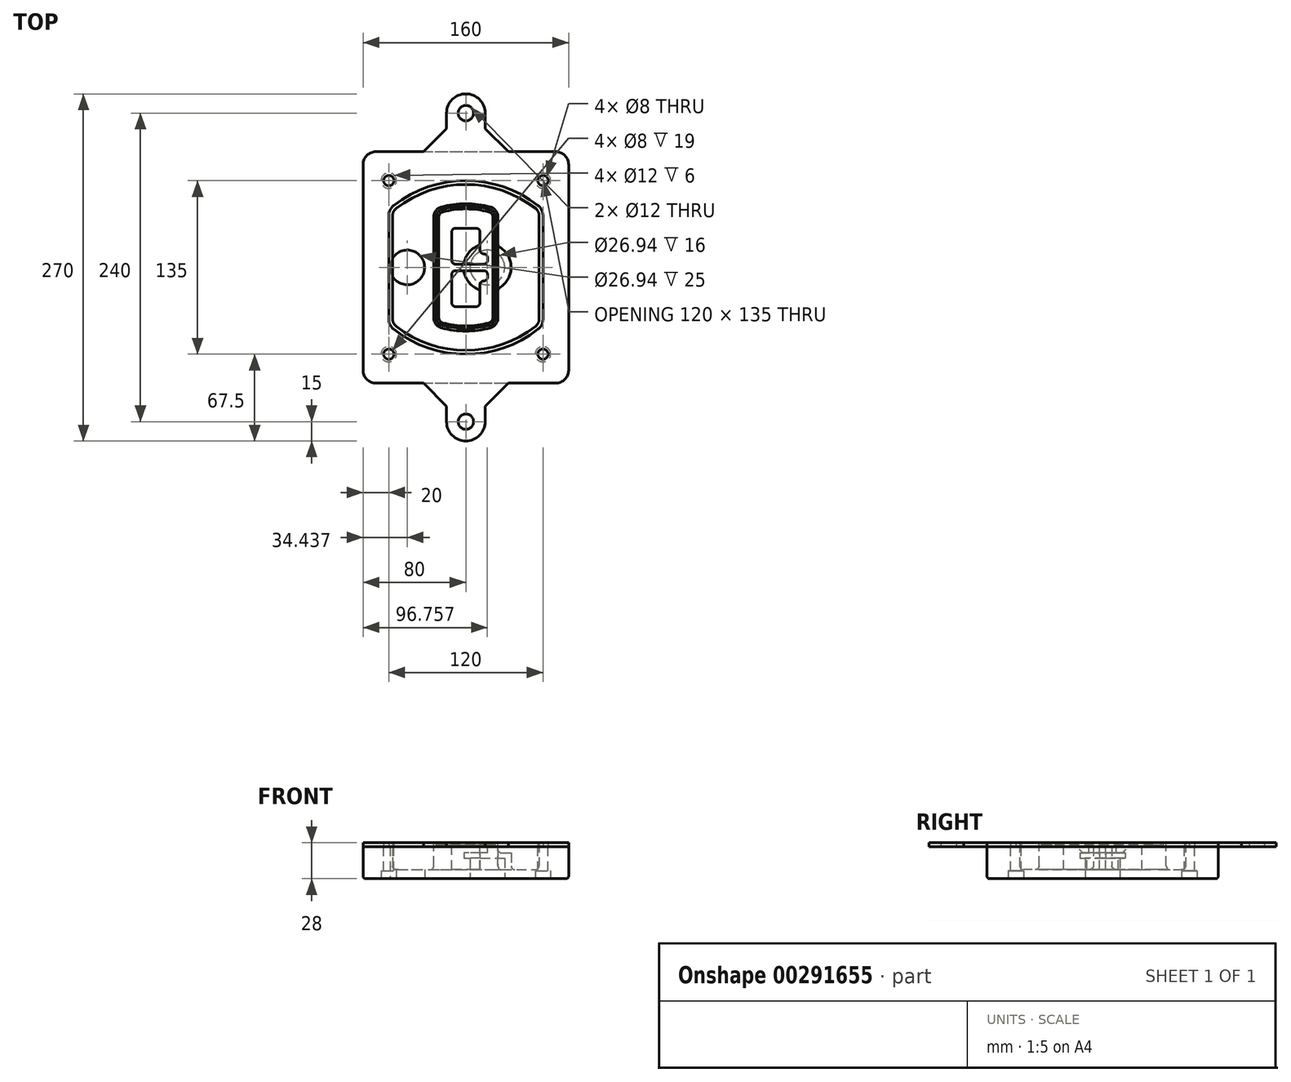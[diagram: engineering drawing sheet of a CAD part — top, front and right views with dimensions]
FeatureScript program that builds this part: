
annotation { "Feature Type Name" : "Feature", "Feature Type Description" : "" }
export const myFeature = defineFeature(function(context is Context, id is Id, definition is map)
    precondition{}
    {
        {
            var Q0;
            Q0=qCreatedBy(makeId("Top.planeOp"),FACE);
            var sketch = newSketch(context, id + "F0", { "sketchPlane" : qUnion([Q0])});
            skPoint(sketch, "E0.rect.middle", {"position": v(0, 0) * mm});
            skLineSegment(sketch, "E1.bottom", {"start": v(-70, -90) * mm, "end": v(70, -90) * mm});
            skLineSegment(sketch, "E1.top", {"start": v(-70, 90) * mm, "end": v(70, 90) * mm});
            skLineSegment(sketch, "E1.left", {"start": v(-80, -80) * mm, "end": v(-80, 80) * mm});
            skLineSegment(sketch, "E1.right", {"start": v(80, -80) * mm, "end": v(80, 80) * mm});
            skLineSegment(sketch, "E2", {"start": v(-80, 90) * mm, "end": v(80, -90) * mm, "construction": true});
            skLineSegment(sketch, "E3", {"start": v(80, 90) * mm, "end": v(-80, -90) * mm, "construction": true});
            skCircle(sketch, "E4", {"center": v(-60, 67.5) * mm, "radius": 4 * mm});
            skCircle(sketch, "E5", {"center": v(60, 67.5) * mm, "radius": 4 * mm});
            skCircle(sketch, "E6", {"center": v(60, -67.5) * mm, "radius": 4 * mm});
            skCircle(sketch, "E7", {"center": v(-60, -67.5) * mm, "radius": 4 * mm});
            skLineSegment(sketch, "E8", {"start": v(-60, 67.5) * mm, "end": v(60, 67.5) * mm, "construction": true});
            skLineSegment(sketch, "E9", {"start": v(60, 67.5) * mm, "end": v(60, -67.5) * mm, "construction": true});
            skLineSegment(sketch, "E10", {"start": v(60, -67.5) * mm, "end": v(-60, -67.5) * mm, "construction": true});
            skLineSegment(sketch, "E11", {"start": v(-60, -67.5) * mm, "end": v(-60, 67.5) * mm, "construction": true});
            skLineSegment(sketch, "E12", {"start": v(-60, 40.3) * mm, "end": v(-60, -40.3) * mm});
            skLineSegment(sketch, "E13", {"start": v(60, 40.3) * mm, "end": v(60, -40.3) * mm});
            skArc(sketch, "E14", {"start": v(56.15, 48.18) * mm, "mid": v(0, 67.5) * mm, "end": v(-56.15, 48.18) * mm});
            skArc(sketch, "E15", {"start": v(-56.15, -48.18) * mm, "mid": v(0, -67.5) * mm, "end": v(56.15, -48.18) * mm});
            skLineSegment(sketch, "E16", {"start": v(-60, 0) * mm, "end": v(60, 0) * mm, "construction": true});
            skPoint(sketch, "E17.visualSharp", {"position": v(-60, -45) * mm});
            skArc(sketch, "E17.filletArc", {"start": v(-60, -40.3) * mm, "mid": v(-58.99, -44.68) * mm, "end": v(-56.15, -48.18) * mm});
            skPoint(sketch, "E18.visualSharp", {"position": v(-60, 45) * mm});
            skArc(sketch, "E18.filletArc", {"start": v(-56.15, 48.18) * mm, "mid": v(-58.99, 44.68) * mm, "end": v(-60, 40.3) * mm});
            skPoint(sketch, "E19.visualSharp", {"position": v(60, 45) * mm});
            skArc(sketch, "E19.filletArc", {"start": v(60, 40.3) * mm, "mid": v(58.99, 44.68) * mm, "end": v(56.15, 48.18) * mm});
            skPoint(sketch, "E20.visualSharp", {"position": v(60, -45) * mm});
            skArc(sketch, "E20.filletArc", {"start": v(56.15, -48.18) * mm, "mid": v(58.99, -44.68) * mm, "end": v(60, -40.3) * mm});
            skPoint(sketch, "E21.visualSharp", {"position": v(-80, 90) * mm});
            skArc(sketch, "E21.filletArc", {"start": v(-70, 90) * mm, "mid": v(-77.07, 87.07) * mm, "end": v(-80, 80) * mm});
            skPoint(sketch, "E22.visualSharp", {"position": v(80, 90) * mm});
            skArc(sketch, "E22.filletArc", {"start": v(80, 80) * mm, "mid": v(77.07, 87.07) * mm, "end": v(70, 90) * mm});
            skPoint(sketch, "E23.visualSharp", {"position": v(80, -90) * mm});
            skArc(sketch, "E23.filletArc", {"start": v(70, -90) * mm, "mid": v(77.07, -87.07) * mm, "end": v(80, -80) * mm});
            skPoint(sketch, "E24.visualSharp", {"position": v(-80, -90) * mm});
            skArc(sketch, "E24.filletArc", {"start": v(-80, -80) * mm, "mid": v(-77.07, -87.07) * mm, "end": v(-70, -90) * mm});
            skArc(sketch, "E25.0", {"start": v(57, 40.3) * mm, "mid": v(56.3, 43.36) * mm, "end": v(54.3, 45.81) * mm});
            skLineSegment(sketch, "E25.1", {"start": v(57, 40.3) * mm, "end": v(57, -40.3) * mm});
            skArc(sketch, "E25.2", {"start": v(54.3, -45.81) * mm, "mid": v(56.3, -43.36) * mm, "end": v(57, -40.3) * mm});
            skArc(sketch, "E25.3", {"start": v(-54.3, -45.81) * mm, "mid": v(0, -64.5) * mm, "end": v(54.3, -45.81) * mm});
            skArc(sketch, "E25.4", {"start": v(-57, -40.3) * mm, "mid": v(-56.3, -43.36) * mm, "end": v(-54.3, -45.81) * mm});
            skArc(sketch, "E25.5", {"start": v(54.3, 45.81) * mm, "mid": v(0, 64.5) * mm, "end": v(-54.3, 45.81) * mm});
            skLineSegment(sketch, "E25.6", {"start": v(-57, 40.3) * mm, "end": v(-57, -40.3) * mm});
            skArc(sketch, "E25.7", {"start": v(-54.3, 45.81) * mm, "mid": v(-56.3, 43.36) * mm, "end": v(-57, 40.3) * mm});
            skArc(sketch, "E26.0", {"start": v(-58.62, 51.33) * mm, "mid": v(-62.58, 46.43) * mm, "end": v(-64, 40.3) * mm});
            skArc(sketch, "E26.1", {"start": v(58.62, 51.33) * mm, "mid": v(0, 71.5) * mm, "end": v(-58.62, 51.33) * mm});
            skArc(sketch, "E26.2", {"start": v(64, 40.3) * mm, "mid": v(62.58, 46.43) * mm, "end": v(58.62, 51.33) * mm});
            skLineSegment(sketch, "E26.3", {"start": v(64, 40.3) * mm, "end": v(64, -40.3) * mm});
            skArc(sketch, "E26.4", {"start": v(58.62, -51.33) * mm, "mid": v(62.58, -46.43) * mm, "end": v(64, -40.3) * mm});
            skLineSegment(sketch, "E26.5", {"start": v(-64, 40.3) * mm, "end": v(-64, -40.3) * mm});
            skArc(sketch, "E26.6", {"start": v(-58.62, -51.33) * mm, "mid": v(0, -71.5) * mm, "end": v(58.62, -51.33) * mm});
            skArc(sketch, "E26.7", {"start": v(-64, -40.3) * mm, "mid": v(-62.58, -46.43) * mm, "end": v(-58.62, -51.33) * mm});
            skSolve(sketch);
        }
        {
            var Q0;
            Q0=makeQuery(id+"F0.imprint","IMPRINT",FACE,{"disambiguationData":[TD([[makeQuery(id+"F0.imprint","IMPRINT",EDGE,{"derivedFrom":sQuery(id+"F0.wireOp",EDGE,"E1.bottom")}),1.0]])]});
            var Q1;
            Q1=makeQuery(id+"F0.imprint","IMPRINT",FACE,{"disambiguationData":[TD([[makeQuery(id+"F0.imprint","IMPRINT",EDGE,{"derivedFrom":sQuery(id+"F0.wireOp",EDGE,"E12")}),1.0]])]});
            var Q2;
            Q2=makeQuery(id+"F0.imprint","IMPRINT",FACE,{"disambiguationData":[TD([[makeQuery(id+"F0.imprint","IMPRINT",EDGE,{"derivedFrom":sQuery(id+"F0.wireOp",EDGE,"E25.0")}),1.0]])]});
            var Q3;
            Q3=makeQuery(id+"F0.imprint","IMPRINT",FACE,{"disambiguationData":[TD([[makeQuery(id+"F0.imprint","IMPRINT",EDGE,{"derivedFrom":sQuery(id+"F0.wireOp",EDGE,"E12")}),-1.0]])]});
            extrude(context, id + "F1", {"entities" : qUnion([Q0, Q1, Q2, Q3]), "oppositeDirection" : true, "depth" : 25 * mm});
        }
        {
            var Q0;
            Q0=makeQuery(id+"F0.imprint","IMPRINT",FACE,{"disambiguationData":[TD([[makeQuery(id+"F0.imprint","IMPRINT",EDGE,{"derivedFrom":sQuery(id+"F0.wireOp",EDGE,"E12")}),1.0]])]});
            extrude(context, id + "F2", {"entities" : qUnion([Q0]), "operationType" : NewBodyOperationType.ADD, "depth" : 3 * mm});
        }
        {
            var Q0;
            Q0=makeQuery(id+"F0.imprint","IMPRINT",FACE,{"disambiguationData":[TD([[makeQuery(id+"F0.imprint","IMPRINT",EDGE,{"derivedFrom":sQuery(id+"F0.wireOp",EDGE,"E25.0")}),1.0]])]});
            extrude(context, id + "F3", {"entities" : qUnion([Q0]), "operationType" : NewBodyOperationType.REMOVE, "oppositeDirection" : true, "depth" : 18 * mm});
        }
        {
            var Q0;
            Q0=makeQuery(id+"F2.opExtrude","CAP_FACE",FACE,{"disambiguationData":[OSD([sQuery(id+"F0.wireOp",EDGE,"E12"),sQuery(id+"F0.wireOp",EDGE,"E13"),sQuery(id+"F0.wireOp",EDGE,"E14"),sQuery(id+"F0.wireOp",EDGE,"E15"),sQuery(id+"F0.wireOp",EDGE,"E17.filletArc"),sQuery(id+"F0.wireOp",EDGE,"E18.filletArc"),sQuery(id+"F0.wireOp",EDGE,"E19.filletArc"),sQuery(id+"F0.wireOp",EDGE,"E20.filletArc"),sQuery(id+"F0.wireOp",EDGE,"E25.0"),sQuery(id+"F0.wireOp",EDGE,"E25.1"),sQuery(id+"F0.wireOp",EDGE,"E25.2"),sQuery(id+"F0.wireOp",EDGE,"E25.3"),sQuery(id+"F0.wireOp",EDGE,"E25.4"),sQuery(id+"F0.wireOp",EDGE,"E25.5"),sQuery(id+"F0.wireOp",EDGE,"E25.6"),sQuery(id+"F0.wireOp",EDGE,"E25.7")])],"isStart":false});
            var sketch = newSketch(context, id + "F4", { "sketchPlane" : qUnion([Q0])});
            skArc(sketch, "E27.0", {"start": v(-19.08, -46.97) * mm, "mid": v(0, -49.5) * mm, "end": v(19.08, -46.97) * mm});
            skArc(sketch, "E28.0", {"start": v(19.08, 46.97) * mm, "mid": v(0, 49.5) * mm, "end": v(-19.08, 46.97) * mm});
            skLineSegment(sketch, "E29", {"start": v(-25, 39.25) * mm, "end": v(-25, -39.25) * mm});
            skLineSegment(sketch, "E30", {"start": v(25, 39.25) * mm, "end": v(25, -39.25) * mm});
            skLineSegment(sketch, "E31", {"start": v(-25, 45.1) * mm, "end": v(25, 45.1) * mm, "construction": true});
            skLineSegment(sketch, "E32", {"start": v(-25, -45.1) * mm, "end": v(25, -45.1) * mm, "construction": true});
            skPoint(sketch, "E33.visualSharp", {"position": v(-25, 45.1) * mm});
            skArc(sketch, "E33.filletArc", {"start": v(-19.08, 46.97) * mm, "mid": v(-23.35, 44.11) * mm, "end": v(-25, 39.25) * mm});
            skPoint(sketch, "E34.visualSharp", {"position": v(25, 45.1) * mm});
            skArc(sketch, "E34.filletArc", {"start": v(25, 39.25) * mm, "mid": v(23.35, 44.11) * mm, "end": v(19.08, 46.97) * mm});
            skPoint(sketch, "E35.visualSharp", {"position": v(25, -45.1) * mm});
            skArc(sketch, "E35.filletArc", {"start": v(19.08, -46.97) * mm, "mid": v(23.35, -44.11) * mm, "end": v(25, -39.25) * mm});
            skPoint(sketch, "E36.visualSharp", {"position": v(-25, -45.1) * mm});
            skArc(sketch, "E36.filletArc", {"start": v(-25, -39.25) * mm, "mid": v(-23.35, -44.11) * mm, "end": v(-19.08, -46.97) * mm});
            skArc(sketch, "E37.0", {"start": v(54.3, 45.81) * mm, "mid": v(0, 64.5) * mm, "end": v(-54.3, 45.81) * mm});
            skArc(sketch, "E37.1", {"start": v(-54.3, 45.81) * mm, "mid": v(-56.3, 43.36) * mm, "end": v(-57, 40.3) * mm});
            skLineSegment(sketch, "E37.2", {"start": v(-57, 40.3) * mm, "end": v(-57, -40.3) * mm});
            skArc(sketch, "E37.3", {"start": v(-57, -40.3) * mm, "mid": v(-56.3, -43.36) * mm, "end": v(-54.3, -45.81) * mm});
            skArc(sketch, "E37.4", {"start": v(-54.3, -45.81) * mm, "mid": v(0, -64.5) * mm, "end": v(54.3, -45.81) * mm});
            skArc(sketch, "E37.5", {"start": v(54.3, -45.81) * mm, "mid": v(56.3, -43.36) * mm, "end": v(57, -40.3) * mm});
            skLineSegment(sketch, "E37.6", {"start": v(57, 40.3) * mm, "end": v(57, -40.3) * mm});
            skArc(sketch, "E37.7", {"start": v(57, 40.3) * mm, "mid": v(56.3, 43.36) * mm, "end": v(54.3, 45.81) * mm});
            skLineSegment(sketch, "E38.0", {"start": v(23, 39.25) * mm, "end": v(23, -39.25) * mm});
            skArc(sketch, "E38.1", {"start": v(18.56, -45.04) * mm, "mid": v(21.76, -42.9) * mm, "end": v(23, -39.25) * mm});
            skArc(sketch, "E38.2", {"start": v(-18.56, -45.04) * mm, "mid": v(0, -47.5) * mm, "end": v(18.56, -45.04) * mm});
            skArc(sketch, "E38.3", {"start": v(-23, -39.25) * mm, "mid": v(-21.76, -42.9) * mm, "end": v(-18.56, -45.04) * mm});
            skLineSegment(sketch, "E38.4", {"start": v(-23, 39.25) * mm, "end": v(-23, -39.25) * mm});
            skArc(sketch, "E38.5", {"start": v(23, 39.25) * mm, "mid": v(21.76, 42.9) * mm, "end": v(18.56, 45.04) * mm});
            skArc(sketch, "E38.6", {"start": v(-18.56, 45.04) * mm, "mid": v(-21.76, 42.9) * mm, "end": v(-23, 39.25) * mm});
            skArc(sketch, "E38.7", {"start": v(18.56, 45.04) * mm, "mid": v(0, 47.5) * mm, "end": v(-18.56, 45.04) * mm});
            skArc(sketch, "E39.0", {"start": v(21, 39.25) * mm, "mid": v(20.18, 41.68) * mm, "end": v(18.04, 43.1) * mm});
            skLineSegment(sketch, "E39.1", {"start": v(21, 39.25) * mm, "end": v(21, -39.25) * mm});
            skArc(sketch, "E39.2", {"start": v(18.04, -43.1) * mm, "mid": v(20.18, -41.68) * mm, "end": v(21, -39.25) * mm});
            skArc(sketch, "E39.3", {"start": v(-18.04, -43.1) * mm, "mid": v(0, -45.5) * mm, "end": v(18.04, -43.1) * mm});
            skArc(sketch, "E39.4", {"start": v(-21, -39.25) * mm, "mid": v(-20.18, -41.68) * mm, "end": v(-18.04, -43.1) * mm});
            skArc(sketch, "E39.5", {"start": v(18.04, 43.1) * mm, "mid": v(0, 45.5) * mm, "end": v(-18.04, 43.1) * mm});
            skLineSegment(sketch, "E39.6", {"start": v(-21, 39.25) * mm, "end": v(-21, -39.25) * mm});
            skArc(sketch, "E39.7", {"start": v(-18.04, 43.1) * mm, "mid": v(-20.18, 41.68) * mm, "end": v(-21, 39.25) * mm});
            skLineSegment(sketch, "E40", {"start": v(-25, 0) * mm, "end": v(25, 0) * mm, "construction": true});
            skLineSegment(sketch, "E41", {"start": v(-11, 5.5) * mm, "end": v(-11, 27.5) * mm});
            skLineSegment(sketch, "E42", {"start": v(-8, 30.5) * mm, "end": v(8, 30.5) * mm});
            skLineSegment(sketch, "E43", {"start": v(11, 27.5) * mm, "end": v(11, 13.5) * mm});
            skLineSegment(sketch, "E44", {"start": v(14, 10.5) * mm, "end": v(14, 10.5) * mm});
            skLineSegment(sketch, "E45", {"start": v(17, 7.5) * mm, "end": v(17, 5.5) * mm});
            skLineSegment(sketch, "E46", {"start": v(14, 2.5) * mm, "end": v(-8, 2.5) * mm});
            skPoint(sketch, "E47.visualSharp", {"position": v(-11, 30.5) * mm});
            skArc(sketch, "E47.filletArc", {"start": v(-8, 30.5) * mm, "mid": v(-10.12, 29.62) * mm, "end": v(-11, 27.5) * mm});
            skPoint(sketch, "E48.visualSharp", {"position": v(11, 30.5) * mm});
            skArc(sketch, "E48.filletArc", {"start": v(11, 27.5) * mm, "mid": v(10.12, 29.62) * mm, "end": v(8, 30.5) * mm});
            skPoint(sketch, "E49.visualSharp", {"position": v(11, 10.5) * mm});
            skArc(sketch, "E49.filletArc", {"start": v(11, 13.5) * mm, "mid": v(11.88, 11.38) * mm, "end": v(14, 10.5) * mm});
            skPoint(sketch, "E50.visualSharp", {"position": v(17, 10.5) * mm});
            skArc(sketch, "E50.filletArc", {"start": v(17, 7.5) * mm, "mid": v(16.12, 9.62) * mm, "end": v(14, 10.5) * mm});
            skPoint(sketch, "E51.visualSharp", {"position": v(17, 2.5) * mm});
            skArc(sketch, "E51.filletArc", {"start": v(14, 2.5) * mm, "mid": v(16.12, 3.38) * mm, "end": v(17, 5.5) * mm});
            skPoint(sketch, "E52.visualSharp", {"position": v(-11, 2.5) * mm});
            skArc(sketch, "E52.filletArc", {"start": v(-11, 5.5) * mm, "mid": v(-10.12, 3.38) * mm, "end": v(-8, 2.5) * mm});
            skLineSegment(sketch, "E53.0.MirrorCS", {"start": v(14, -2.5) * mm, "end": v(-8, -2.5) * mm});
            skArc(sketch, "E54.0.MirrorCS", {"start": v(-11, -5.5) * mm, "mid": v(-10.12, -3.38) * mm, "end": v(-8, -2.5) * mm});
            skLineSegment(sketch, "E55.0.MirrorCS", {"start": v(-11, -5.5) * mm, "end": v(-11, -27.5) * mm});
            skArc(sketch, "E56.0.MirrorCS", {"start": v(-8, -30.5) * mm, "mid": v(-10.12, -29.62) * mm, "end": v(-11, -27.5) * mm});
            skLineSegment(sketch, "E57.0.MirrorCS", {"start": v(-8, -30.5) * mm, "end": v(8, -30.5) * mm});
            skArc(sketch, "E58.0.MirrorCS", {"start": v(11, -27.5) * mm, "mid": v(10.12, -29.62) * mm, "end": v(8, -30.5) * mm});
            skLineSegment(sketch, "E59.0.MirrorCS", {"start": v(11, -27.5) * mm, "end": v(11, -13.5) * mm});
            skArc(sketch, "E60.0.MirrorCS", {"start": v(11, -13.5) * mm, "mid": v(11.88, -11.38) * mm, "end": v(14, -10.5) * mm});
            skArc(sketch, "E61.0.MirrorCS", {"start": v(17, -7.5) * mm, "mid": v(16.12, -9.62) * mm, "end": v(14, -10.5) * mm});
            skLineSegment(sketch, "E62.0.MirrorCS", {"start": v(17, -7.5) * mm, "end": v(17, -5.5) * mm});
            skArc(sketch, "E63.0.MirrorCS", {"start": v(14, -2.5) * mm, "mid": v(16.12, -3.38) * mm, "end": v(17, -5.5) * mm});
            skSolve(sketch);
        }
        {
            var Q0;
            Q0=makeQuery(id+"F4.imprint","IMPRINT",FACE,{"disambiguationData":[TD([[makeQuery(id+"F4.imprint","IMPRINT",EDGE,{"derivedFrom":sQuery(id+"F4.wireOp",EDGE,"E27.0")}),1.0]])]});
            var Q1;
            Q1=makeQuery(id+"F4.imprint","IMPRINT",FACE,{"disambiguationData":[TD([[makeQuery(id+"F4.imprint","IMPRINT",EDGE,{"derivedFrom":sQuery(id+"F4.wireOp",EDGE,"E38.0")}),-1.0]])]});
            var Q2;
            Q2=makeQuery(id+"F4.imprint","IMPRINT",FACE,{"disambiguationData":[TD([[makeQuery(id+"F4.imprint","IMPRINT",EDGE,{"derivedFrom":sQuery(id+"F4.wireOp",EDGE,"E39.0")}),1.0]])]});
            extrude(context, id + "F5", {"entities" : qUnion([Q0, Q1, Q2]), "operationType" : NewBodyOperationType.ADD, "endBound" : BoundingType.UP_TO_NEXT, "oppositeDirection" : true, "depth" : 25 * mm});
        }
        {
            var Q0;
            Q0=makeQuery(id+"F4.imprint","IMPRINT",FACE,{"disambiguationData":[TD([[makeQuery(id+"F4.imprint","IMPRINT",EDGE,{"derivedFrom":sQuery(id+"F4.wireOp",EDGE,"E38.0")}),-1.0]])]});
            extrude(context, id + "F6", {"entities" : qUnion([Q0]), "operationType" : NewBodyOperationType.REMOVE, "oppositeDirection" : true, "depth" : 2 * mm});
        }
        {
            var Q0;
            Q0=makeQuery(id+"F1.opExtrude","CAP_FACE",FACE,{"disambiguationData":[OSD([sQuery(id+"F0.wireOp",EDGE,"E1.bottom"),sQuery(id+"F0.wireOp",EDGE,"E1.top"),sQuery(id+"F0.wireOp",EDGE,"E1.left"),sQuery(id+"F0.wireOp",EDGE,"E1.right"),sQuery(id+"F0.wireOp",EDGE,"E4"),sQuery(id+"F0.wireOp",EDGE,"E5"),sQuery(id+"F0.wireOp",EDGE,"E6"),sQuery(id+"F0.wireOp",EDGE,"E7"),sQuery(id+"F0.wireOp",EDGE,"E21.filletArc"),sQuery(id+"F0.wireOp",EDGE,"E22.filletArc"),sQuery(id+"F0.wireOp",EDGE,"E23.filletArc"),sQuery(id+"F0.wireOp",EDGE,"E24.filletArc")])],"isStart":false});
            var sketch = newSketch(context, id + "F7", { "sketchPlane" : qUnion([Q0])});
            skCircle(sketch, "E64", {"center": v(16.76, 0) * mm, "radius": 13.47 * mm});
            skCircle(sketch, "E65", {"center": v(-45.56, 0) * mm, "radius": 13.47 * mm});
            skLineSegment(sketch, "E66", {"start": v(80, 0) * mm, "end": v(-80, 0) * mm});
            skCircle(sketch, "E67", {"center": v(16.76, 0) * mm, "radius": 18.47 * mm});
            skCircle(sketch, "E68", {"center": v(60, -67.5) * mm, "radius": 6 * mm});
            skCircle(sketch, "E69", {"center": v(-60, -67.5) * mm, "radius": 6 * mm});
            skCircle(sketch, "E70", {"center": v(-60, 67.5) * mm, "radius": 6 * mm});
            skCircle(sketch, "E71", {"center": v(60, 67.5) * mm, "radius": 6 * mm});
            skSolve(sketch);
        }
        {
            var Q0;
            {var subQ1=sQuery(id+"F7.wireOp",EDGE,"E66");var subQ4=sQuery(id+"F7.wireOp",EDGE,"E64");var subQ6=makeQuery(id+"F7.imprint","INTERSECT",VERTEX,{"disambiguationData":[OD(0.0)],"derivedFrom":[subQ4,subQ1]});Q0=makeQuery(id+"F7.imprint","IMPRINT",FACE,{"disambiguationData":[TD([[makeQuery(id+"F7.imprint","IMPRINT",EDGE,{"disambiguationData":[TD([[subQ6,-1.0]])],"derivedFrom":subQ4}),-1.0]])]});}
            var Q1;
            {var subQ0=sQuery(id+"F7.wireOp",EDGE,"E66");var subQ1=sQuery(id+"F7.wireOp",EDGE,"E64");var subQ3=makeQuery(id+"F7.imprint","INTERSECT",VERTEX,{"disambiguationData":[OD(0.0)],"derivedFrom":[subQ1,subQ0]});Q1=makeQuery(id+"F7.imprint","IMPRINT",FACE,{"disambiguationData":[TD([[makeQuery(id+"F7.imprint","IMPRINT",EDGE,{"disambiguationData":[TD([[subQ3,-1.0]])],"derivedFrom":subQ1}),1.0]])]});}
            var Q2;
            {var subQ0=sQuery(id+"F7.wireOp",EDGE,"E66");var subQ1=sQuery(id+"F7.wireOp",EDGE,"E64");var subQ3=makeQuery(id+"F7.imprint","INTERSECT",VERTEX,{"disambiguationData":[OD(0.0)],"derivedFrom":[subQ1,subQ0]});Q2=makeQuery(id+"F7.imprint","IMPRINT",FACE,{"disambiguationData":[TD([[makeQuery(id+"F7.imprint","IMPRINT",EDGE,{"disambiguationData":[TD([[subQ3,1.0]])],"derivedFrom":subQ1}),1.0]])]});}
            var Q3;
            {var subQ1=sQuery(id+"F7.wireOp",EDGE,"E66");var subQ4=sQuery(id+"F7.wireOp",EDGE,"E64");var subQ6=makeQuery(id+"F7.imprint","INTERSECT",VERTEX,{"disambiguationData":[OD(0.0)],"derivedFrom":[subQ4,subQ1]});Q3=makeQuery(id+"F7.imprint","IMPRINT",FACE,{"disambiguationData":[TD([[makeQuery(id+"F7.imprint","IMPRINT",EDGE,{"disambiguationData":[TD([[subQ6,1.0]])],"derivedFrom":subQ4}),-1.0]])]});}
            extrude(context, id + "F8", {"entities" : qUnion([Q0, Q1, Q2, Q3]), "operationType" : NewBodyOperationType.ADD, "oppositeDirection" : true, "depth" : 20 * mm});
        }
        {
            var Q0;
            {var subQ0=sQuery(id+"F7.wireOp",EDGE,"E66");var subQ1=sQuery(id+"F7.wireOp",EDGE,"E64");var subQ3=makeQuery(id+"F7.imprint","INTERSECT",VERTEX,{"disambiguationData":[OD(0.0)],"derivedFrom":[subQ1,subQ0]});Q0=makeQuery(id+"F7.imprint","IMPRINT",FACE,{"disambiguationData":[TD([[makeQuery(id+"F7.imprint","IMPRINT",EDGE,{"disambiguationData":[TD([[subQ3,-1.0]])],"derivedFrom":subQ1}),1.0]])]});}
            var Q1;
            {var subQ0=sQuery(id+"F7.wireOp",EDGE,"E66");var subQ1=sQuery(id+"F7.wireOp",EDGE,"E64");var subQ3=makeQuery(id+"F7.imprint","INTERSECT",VERTEX,{"disambiguationData":[OD(0.0)],"derivedFrom":[subQ1,subQ0]});Q1=makeQuery(id+"F7.imprint","IMPRINT",FACE,{"disambiguationData":[TD([[makeQuery(id+"F7.imprint","IMPRINT",EDGE,{"disambiguationData":[TD([[subQ3,1.0]])],"derivedFrom":subQ1}),1.0]])]});}
            extrude(context, id + "F9", {"entities" : qUnion([Q0, Q1]), "operationType" : NewBodyOperationType.REMOVE, "oppositeDirection" : true, "depth" : 16 * mm});
        }
        {
            var Q0;
            {var subQ0=sQuery(id+"F7.wireOp",EDGE,"E66");var subQ1=sQuery(id+"F7.wireOp",EDGE,"E65");var subQ3=makeQuery(id+"F7.imprint","INTERSECT",VERTEX,{"disambiguationData":[OD(0.0)],"derivedFrom":[subQ1,subQ0]});Q0=makeQuery(id+"F7.imprint","IMPRINT",FACE,{"disambiguationData":[TD([[makeQuery(id+"F7.imprint","IMPRINT",EDGE,{"disambiguationData":[TD([[subQ3,-1.0]])],"derivedFrom":subQ1}),1.0]])]});}
            var Q1;
            {var subQ0=sQuery(id+"F7.wireOp",EDGE,"E66");var subQ1=sQuery(id+"F7.wireOp",EDGE,"E65");var subQ3=makeQuery(id+"F7.imprint","INTERSECT",VERTEX,{"disambiguationData":[OD(0.0)],"derivedFrom":[subQ1,subQ0]});Q1=makeQuery(id+"F7.imprint","IMPRINT",FACE,{"disambiguationData":[TD([[makeQuery(id+"F7.imprint","IMPRINT",EDGE,{"disambiguationData":[TD([[subQ3,1.0]])],"derivedFrom":subQ1}),1.0]])]});}
            extrude(context, id + "F10", {"entities" : qUnion([Q0, Q1]), "operationType" : NewBodyOperationType.REMOVE, "oppositeDirection" : true, "depth" : 25 * mm});
        }
        {
            var Q0;
            Q0=makeQuery(id+"F7.imprint","IMPRINT",FACE,{"disambiguationData":[TD([[makeQuery(id+"F7.imprint","IMPRINT",EDGE,{"derivedFrom":sQuery(id+"F7.wireOp",EDGE,"E68")}),1.0]])]});
            var Q1;
            Q1=makeQuery(id+"F7.imprint","IMPRINT",FACE,{"disambiguationData":[TD([[makeQuery(id+"F7.imprint","IMPRINT",EDGE,{"derivedFrom":makeQuery(id+"F1.opExtrude","CAP_EDGE",EDGE,{"disambiguationData":[OSD([sQuery(id+"F0.wireOp",EDGE,"E5")])],"isStart":false})}),-1.0]])]});
            var Q2;
            Q2=makeQuery(id+"F7.imprint","IMPRINT",FACE,{"disambiguationData":[TD([[makeQuery(id+"F7.imprint","IMPRINT",EDGE,{"derivedFrom":sQuery(id+"F7.wireOp",EDGE,"E69")}),1.0]])]});
            var Q3;
            Q3=makeQuery(id+"F7.imprint","IMPRINT",FACE,{"disambiguationData":[TD([[makeQuery(id+"F7.imprint","IMPRINT",EDGE,{"derivedFrom":makeQuery(id+"F1.opExtrude","CAP_EDGE",EDGE,{"disambiguationData":[OSD([sQuery(id+"F0.wireOp",EDGE,"E4")])],"isStart":false})}),-1.0]])]});
            var Q4;
            Q4=makeQuery(id+"F7.imprint","IMPRINT",FACE,{"disambiguationData":[TD([[makeQuery(id+"F7.imprint","IMPRINT",EDGE,{"derivedFrom":sQuery(id+"F7.wireOp",EDGE,"E70")}),1.0]])]});
            var Q5;
            Q5=makeQuery(id+"F7.imprint","IMPRINT",FACE,{"disambiguationData":[TD([[makeQuery(id+"F7.imprint","IMPRINT",EDGE,{"derivedFrom":makeQuery(id+"F1.opExtrude","CAP_EDGE",EDGE,{"disambiguationData":[OSD([sQuery(id+"F0.wireOp",EDGE,"E7")])],"isStart":false})}),-1.0]])]});
            var Q6;
            Q6=makeQuery(id+"F7.imprint","IMPRINT",FACE,{"disambiguationData":[TD([[makeQuery(id+"F7.imprint","IMPRINT",EDGE,{"derivedFrom":sQuery(id+"F7.wireOp",EDGE,"E71")}),1.0]])]});
            var Q7;
            Q7=makeQuery(id+"F7.imprint","IMPRINT",FACE,{"disambiguationData":[TD([[makeQuery(id+"F7.imprint","IMPRINT",EDGE,{"derivedFrom":makeQuery(id+"F1.opExtrude","CAP_EDGE",EDGE,{"disambiguationData":[OSD([sQuery(id+"F0.wireOp",EDGE,"E6")])],"isStart":false})}),-1.0]])]});
            extrude(context, id + "F11", {"entities" : qUnion([Q0, Q1, Q2, Q3, Q4, Q5, Q6, Q7]), "operationType" : NewBodyOperationType.REMOVE, "oppositeDirection" : true, "depth" : 6 * mm});
        }
        {
            var Q0;
            Q0=makeQuery(id+"F9.boolean.opBoolean","COPY",FACE,{"derivedFrom":makeQuery(id+"F9.opExtrude","CAP_FACE",FACE,{"disambiguationData":[OSD([sQuery(id+"F7.wireOp",EDGE,"E64")])],"isStart":false})});
            var sketch = newSketch(context, id + "F12", { "sketchPlane" : qUnion([Q0])});
            skArc(sketch, "E72.0", {"start": v(11, 17.55) * mm, "mid": v(2.57, 11.82) * mm, "end": v(-1.54, 2.5) * mm});
            skArc(sketch, "E72.1", {"start": v(-1.54, -2.5) * mm, "mid": v(2.57, -11.82) * mm, "end": v(11, -17.55) * mm});
            skLineSegment(sketch, "E73", {"start": v(-1.54, -2.5) * mm, "end": v(14, -2.5) * mm});
            skLineSegment(sketch, "E74.0", {"start": v(14, 2.5) * mm, "end": v(-1.54, 2.5) * mm});
            skArc(sketch, "E74.1", {"start": v(14, 2.5) * mm, "mid": v(16.12, 3.38) * mm, "end": v(17, 5.5) * mm});
            skLineSegment(sketch, "E74.2", {"start": v(17, 7.5) * mm, "end": v(17, 5.5) * mm});
            skArc(sketch, "E74.3", {"start": v(17, 7.5) * mm, "mid": v(16.12, 9.62) * mm, "end": v(14, 10.5) * mm});
            skArc(sketch, "E74.4", {"start": v(11, 13.5) * mm, "mid": v(11.88, 11.38) * mm, "end": v(14, 10.5) * mm});
            skLineSegment(sketch, "E74.5", {"start": v(11, 17.55) * mm, "end": v(11, 13.5) * mm});
            skLineSegment(sketch, "E74.7", {"start": v(14, -2.5) * mm, "end": v(-1.54, -2.5) * mm});
            skArc(sketch, "E74.8", {"start": v(14, -2.5) * mm, "mid": v(16.12, -3.38) * mm, "end": v(17, -5.5) * mm});
            skLineSegment(sketch, "E74.9", {"start": v(17, -7.5) * mm, "end": v(17, -5.5) * mm});
            skArc(sketch, "E74.10", {"start": v(17, -7.5) * mm, "mid": v(16.12, -9.62) * mm, "end": v(14, -10.5) * mm});
            skArc(sketch, "E74.11", {"start": v(11, -13.5) * mm, "mid": v(11.88, -11.38) * mm, "end": v(14, -10.5) * mm});
            skLineSegment(sketch, "E74.12", {"start": v(11, -17.55) * mm, "end": v(11, -13.5) * mm});
            skPoint(sketch, "E75.orphan", {"position": v(11, -27.5) * mm});
            skPoint(sketch, "E76.orphan", {"position": v(-8, -2.5) * mm});
            skPoint(sketch, "E77.orphan", {"position": v(-8, 2.5) * mm});
            skPoint(sketch, "E78.orphan", {"position": v(11, 27.5) * mm});
            skSolve(sketch);
        }
        {
            var Q0;
            {var subQ7=sQuery(id+"F12.wireOp",EDGE,"E72.0");var subQ14=sQuery(id+"F12.wireOp",EDGE,"E72.1");var subQ16=sQuery(id+"F12.wireOp",EDGE,"E74.1");var subQ18=sQuery(id+"F12.wireOp",EDGE,"E74.8");Q0=qUnion([makeQuery(id+"F12.imprint","IMPRINT",FACE,{"disambiguationData":[TD([[makeQuery(id+"F12.imprint","IMPRINT",EDGE,{"derivedFrom":subQ7}),1.0]])]}),makeQuery(id+"F12.imprint","IMPRINT",FACE,{"disambiguationData":[TD([[makeQuery(id+"F12.imprint","IMPRINT",EDGE,{"derivedFrom":subQ14}),1.0]])]}),makeQuery(id+"F12.imprint","IMPRINT",FACE,{"disambiguationData":[TD([[makeQuery(id+"F12.imprint","IMPRINT",EDGE,{"derivedFrom":subQ16}),1.0]])]}),makeQuery(id+"F12.imprint","IMPRINT",FACE,{"disambiguationData":[TD([[makeQuery(id+"F12.imprint","IMPRINT",EDGE,{"derivedFrom":subQ18}),-1.0]])]})]);}
            var Q1;
            Q1=makeQuery(id+"F5.boolean.opBoolean","SPLIT",FACE,{"disambiguationData":[TD([makeQuery(id+"F5.opExtrude","SWEPT_FACE",FACE,{"disambiguationData":[OSD([sQuery(id+"F4.wireOp",EDGE,"E41")])]})])],"derivedFrom":makeQuery(id+"F3.boolean.opBoolean","COPY",FACE,{"derivedFrom":makeQuery(id+"F3.opExtrude","CAP_FACE",FACE,{"disambiguationData":[OSD([sQuery(id+"F0.wireOp",EDGE,"E25.0"),sQuery(id+"F0.wireOp",EDGE,"E25.1"),sQuery(id+"F0.wireOp",EDGE,"E25.2"),sQuery(id+"F0.wireOp",EDGE,"E25.3"),sQuery(id+"F0.wireOp",EDGE,"E25.4"),sQuery(id+"F0.wireOp",EDGE,"E25.5"),sQuery(id+"F0.wireOp",EDGE,"E25.6"),sQuery(id+"F0.wireOp",EDGE,"E25.7")])],"isStart":false})})});
            extrude(context, id + "F13", {"entities" : qUnion([Q0]), "operationType" : NewBodyOperationType.REMOVE, "endBound" : BoundingType.UP_TO_SURFACE, "endBoundEntityFace" : qUnion([Q1]), "depth" : 25 * mm});
        }
        {
            var Q0;
            Q0=makeQuery(id+"F3.boolean.opBoolean","COPY",EDGE,{"derivedFrom":makeQuery(id+"F3.opExtrude","CAP_EDGE",EDGE,{"disambiguationData":[OSD([sQuery(id+"F0.wireOp",EDGE,"E25.6")])],"isStart":false})});
            var Q1;
            Q1=makeQuery(id+"F8.boolean.opBoolean","INTERSECT",EDGE,{"derivedFrom":[makeQuery(id+"F5.opExtrude","SWEPT_FACE",FACE,{"disambiguationData":[OSD([sQuery(id+"F4.wireOp",EDGE,"E30")])]}),makeQuery(id+"F8.opExtrude","CAP_FACE",FACE,{"disambiguationData":[OSD([sQuery(id+"F7.wireOp",EDGE,"E67")])],"isStart":false})]});
            var Q2;
            Q2=makeQuery(id+"F8.boolean.opBoolean","INTERSECT",EDGE,{"disambiguationData":[OD(1.0)],"derivedFrom":[makeQuery(id+"F5.opExtrude","SWEPT_FACE",FACE,{"disambiguationData":[OSD([sQuery(id+"F4.wireOp",EDGE,"E30")])]}),makeQuery(id+"F8.opExtrude","SWEPT_FACE",FACE,{"disambiguationData":[OSD([sQuery(id+"F7.wireOp",EDGE,"E67")])]})]});
            var Q3;
            {var subQ0=sQuery(id+"F4.wireOp",EDGE,"E30");Q3=makeQuery(id+"F8.boolean.opBoolean","SPLIT",EDGE,{"disambiguationData":[TD([makeQuery(id+"F5.opExtrude","SWEPT_FACE",FACE,{"disambiguationData":[OSD([sQuery(id+"F4.wireOp",EDGE,"E35.filletArc")])]})])],"derivedFrom":makeQuery(id+"F5.opExtrude","CAP_EDGE",EDGE,{"disambiguationData":[OSD([subQ0])],"isStart":false})});}
            var Q4;
            {var subQ0=sQuery(id+"F0.wireOp",EDGE,"E25.7");var subQ1=sQuery(id+"F0.wireOp",EDGE,"E25.1");var subQ2=sQuery(id+"F0.wireOp",EDGE,"E25.6");var subQ3=sQuery(id+"F0.wireOp",EDGE,"E25.5");var subQ4=sQuery(id+"F0.wireOp",EDGE,"E25.4");var subQ5=sQuery(id+"F0.wireOp",EDGE,"E25.0");var subQ6=sQuery(id+"F0.wireOp",EDGE,"E25.2");var subQ7=sQuery(id+"F0.wireOp",EDGE,"E25.3");Q4=makeQuery(id+"F8.boolean.opBoolean","INTERSECT",EDGE,{"derivedFrom":[makeQuery(id+"F5.boolean.opBoolean","SPLIT",FACE,{"disambiguationData":[TD([makeQuery(id+"F2.opExtrude","SWEPT_FACE",FACE,{"disambiguationData":[OSD([subQ5])]})])],"derivedFrom":makeQuery(id+"F3.boolean.opBoolean","COPY",FACE,{"derivedFrom":makeQuery(id+"F3.opExtrude","CAP_FACE",FACE,{"disambiguationData":[OSD([subQ5,subQ1,subQ6,subQ7,subQ4,subQ3,subQ2,subQ0])],"isStart":false})})}),makeQuery(id+"F8.opExtrude","SWEPT_FACE",FACE,{"disambiguationData":[OSD([sQuery(id+"F7.wireOp",EDGE,"E67")])]})]});}
            var Q5;
            Q5=makeQuery(id+"F8.boolean.opBoolean","INTERSECT",EDGE,{"disambiguationData":[OD(0.0)],"derivedFrom":[makeQuery(id+"F5.opExtrude","SWEPT_FACE",FACE,{"disambiguationData":[OSD([sQuery(id+"F4.wireOp",EDGE,"E30")])]}),makeQuery(id+"F8.opExtrude","SWEPT_FACE",FACE,{"disambiguationData":[OSD([sQuery(id+"F7.wireOp",EDGE,"E67")])]})]});
            fillet(context, id + "F14", {"entities" : qUnion([Q0, Q1, Q2, Q3, Q4, Q5]), "radius" : 3 * mm, "tangentPropagation" : true, "allowEdgeOverflow" : false});
        }
        {
            var Q0;
            Q0=makeQuery(id+"F1.opExtrude","CAP_EDGE",EDGE,{"disambiguationData":[OSD([sQuery(id+"F0.wireOp",EDGE,"E1.bottom")])],"isStart":false});
            fillet(context, id + "F15", {"entities" : qUnion([Q0]), "radius" : 2 * mm, "tangentPropagation" : true, "allowEdgeOverflow" : false});
        }
        {
            var Q0;
            {var subQ0=sQuery(id+"F0.wireOp",EDGE,"E21.filletArc");var subQ1=sQuery(id+"F0.wireOp",EDGE,"E7");var subQ2=sQuery(id+"F0.wireOp",EDGE,"E6");var subQ3=sQuery(id+"F0.wireOp",EDGE,"E5");var subQ4=sQuery(id+"F0.wireOp",EDGE,"E4");var subQ5=sQuery(id+"F0.wireOp",EDGE,"E22.filletArc");var subQ6=sQuery(id+"F0.wireOp",EDGE,"E1.bottom");var subQ7=sQuery(id+"F0.wireOp",EDGE,"E1.right");var subQ8=sQuery(id+"F0.wireOp",EDGE,"E1.top");var subQ9=sQuery(id+"F0.wireOp",EDGE,"E1.left");var subQ10=sQuery(id+"F0.wireOp",EDGE,"E23.filletArc");var subQ11=sQuery(id+"F0.wireOp",EDGE,"E24.filletArc");Q0=makeQuery(id+"F2.boolean.opBoolean","SPLIT",FACE,{"disambiguationData":[TD([makeQuery(id+"F1.opExtrude","SWEPT_FACE",FACE,{"disambiguationData":[OSD([subQ6])]})])],"derivedFrom":makeQuery(id+"F1.opExtrude","CAP_FACE",FACE,{"disambiguationData":[OSD([subQ6,subQ8,subQ9,subQ7,subQ4,subQ3,subQ2,subQ1,subQ0,subQ5,subQ10,subQ11])],"isStart":true})});}
            var sketch = newSketch(context, id + "F16", { "sketchPlane" : qUnion([Q0])});
            skArc(sketch, "E79.0", {"start": v(56.15, 48.18) * mm, "mid": v(0, 67.5) * mm, "end": v(-56.15, 48.18) * mm});
            skLineSegment(sketch, "E79.1", {"start": v(-70, 90) * mm, "end": v(70, 90) * mm});
            skArc(sketch, "E79.2", {"start": v(-70, 90) * mm, "mid": v(-77.07, 87.07) * mm, "end": v(-80, 80) * mm});
            skCircle(sketch, "E79.3", {"center": v(60, -67.5) * mm, "radius": 4 * mm});
            skLineSegment(sketch, "E79.5", {"start": v(-80, -80) * mm, "end": v(-80, 80) * mm});
            skLineSegment(sketch, "E79.6", {"start": v(-70, -90) * mm, "end": v(70, -90) * mm});
            skArc(sketch, "E79.7", {"start": v(-80, -80) * mm, "mid": v(-77.07, -87.07) * mm, "end": v(-70, -90) * mm});
            skLineSegment(sketch, "E80", {"start": v(0, 90) * mm, "end": v(0, 120) * mm, "construction": true});
            skPoint(sketch, "E80.endSnap0", {"position": v(0, 67.5) * mm});
            skCircle(sketch, "E81", {"center": v(0, 120) * mm, "radius": 6 * mm});
            skArc(sketch, "E82", {"start": v(15, 120) * mm, "mid": v(0, 135) * mm, "end": v(-15, 120) * mm});
            skLineSegment(sketch, "E83", {"start": v(-15, 120) * mm, "end": v(-15, 108) * mm});
            skLineSegment(sketch, "E84", {"start": v(-15, 108) * mm, "end": v(-33, 90) * mm});
            skLineSegment(sketch, "E85", {"start": v(15, 120) * mm, "end": v(15, 108) * mm});
            skLineSegment(sketch, "E86", {"start": v(15, 108) * mm, "end": v(33, 90) * mm});
            skLineSegment(sketch, "E87", {"start": v(80, 0) * mm, "end": v(-80, 0) * mm, "construction": true});
            skLineSegment(sketch, "E88.MirrorCS", {"start": v(15, -120) * mm, "end": v(15, -108) * mm});
            skLineSegment(sketch, "E89.MirrorCS", {"start": v(-15, -108) * mm, "end": v(-33, -90) * mm});
            skLineSegment(sketch, "E90.MirrorCS", {"start": v(-15, -120) * mm, "end": v(-15, -108) * mm});
            skArc(sketch, "E91.MirrorCS", {"start": v(15, -120) * mm, "mid": v(0, -135) * mm, "end": v(-15, -120) * mm});
            skLineSegment(sketch, "E92.MirrorCS", {"start": v(15, -108) * mm, "end": v(33, -90) * mm});
            skCircle(sketch, "E93.MirrorC", {"center": v(0, -120) * mm, "radius": 6 * mm});
            skLineSegment(sketch, "E94.MirrorCS", {"start": v(0, -90) * mm, "end": v(0, -120) * mm, "construction": true});
            skSolve(sketch);
        }
        {
            var Q0;
            Q0=makeQuery(id+"F16.imprint","IMPRINT",FACE,{"disambiguationData":[TD([[makeQuery(id+"F16.imprint","IMPRINT",EDGE,{"derivedFrom":sQuery(id+"F16.wireOp",EDGE,"E79.0")}),-1.0]])]});
            var Q1;
            Q1=makeQuery(id+"F16.imprint","IMPRINT",FACE,{"disambiguationData":[TD([[makeQuery(id+"F16.imprint","IMPRINT",EDGE,{"derivedFrom":sQuery(id+"F16.wireOp",EDGE,"E81")}),-1.0]])]});
            var Q2;
            Q2=makeQuery(id+"F16.imprint","IMPRINT",FACE,{"disambiguationData":[TD([[makeQuery(id+"F16.imprint","IMPRINT",EDGE,{"derivedFrom":sQuery(id+"F16.wireOp",EDGE,"E88.MirrorCS")}),1.0]])]});
            var Q3;
            Q3=makeQuery(id+"F2.opExtrude","CAP_FACE",FACE,{"disambiguationData":[OSD([sQuery(id+"F0.wireOp",EDGE,"E12"),sQuery(id+"F0.wireOp",EDGE,"E13"),sQuery(id+"F0.wireOp",EDGE,"E14"),sQuery(id+"F0.wireOp",EDGE,"E15"),sQuery(id+"F0.wireOp",EDGE,"E17.filletArc"),sQuery(id+"F0.wireOp",EDGE,"E18.filletArc"),sQuery(id+"F0.wireOp",EDGE,"E19.filletArc"),sQuery(id+"F0.wireOp",EDGE,"E20.filletArc"),sQuery(id+"F0.wireOp",EDGE,"E25.0"),sQuery(id+"F0.wireOp",EDGE,"E25.1"),sQuery(id+"F0.wireOp",EDGE,"E25.2"),sQuery(id+"F0.wireOp",EDGE,"E25.3"),sQuery(id+"F0.wireOp",EDGE,"E25.4"),sQuery(id+"F0.wireOp",EDGE,"E25.5"),sQuery(id+"F0.wireOp",EDGE,"E25.6"),sQuery(id+"F0.wireOp",EDGE,"E25.7")])],"isStart":false});
            extrude(context, id + "F17", {"entities" : qUnion([Q0, Q1, Q2]), "endBound" : BoundingType.UP_TO_SURFACE, "endBoundEntityFace" : qUnion([Q3]), "depth" : 25 * mm});
        }
    });
